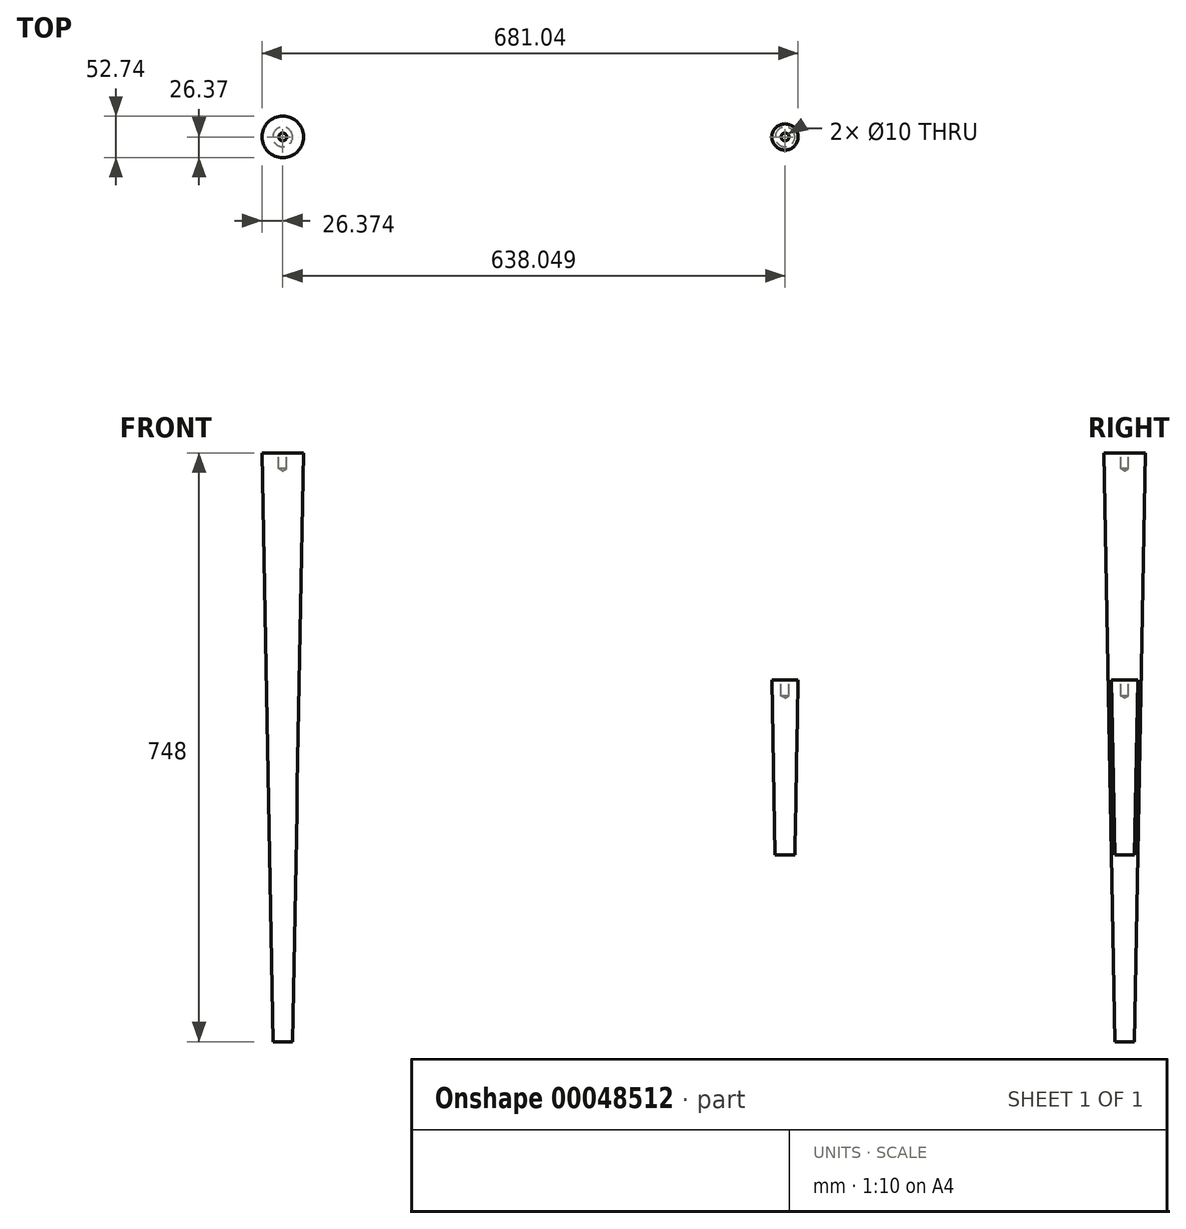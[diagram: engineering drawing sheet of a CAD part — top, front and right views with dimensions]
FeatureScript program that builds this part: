
annotation { "Feature Type Name" : "Feature", "Feature Type Description" : "" }
export const myFeature = defineFeature(function(context is Context, id is Id, definition is map)
    precondition{}
    {
        {
            var Q0;
            Q0=qCreatedBy(makeId("Front.planeOp"),FACE);
            var sketch = newSketch(context, id + "F0", { "sketchPlane" : qUnion([Q0])});
            skLineSegment(sketch, "E0.bottom", {"start": v(-272.94, 167.73) * mm, "end": v(-222.94, 167.73) * mm});
            skLineSegment(sketch, "E0.top", {"start": v(-272.94, -506.27) * mm, "end": v(-222.94, -506.27) * mm});
            skLineSegment(sketch, "E0.left", {"start": v(-272.94, 167.73) * mm, "end": v(-272.94, -506.27) * mm});
            skLineSegment(sketch, "E0.right", {"start": v(-222.94, 167.73) * mm, "end": v(-222.94, -506.27) * mm});
            skLineSegment(sketch, "E1", {"start": v(-247.94, 167.73) * mm, "end": v(-247.94, -506.27) * mm});
            skLineSegment(sketch, "E2", {"start": v(-247.94, -506.27) * mm, "end": v(-260.44, -506.27) * mm});
            skLineSegment(sketch, "E3", {"start": v(-272.94, 167.73) * mm, "end": v(-260.44, -506.27) * mm});
            skLineSegment(sketch, "E4.top", {"start": v(-272.94, 241.73) * mm, "end": v(-222.94, 241.73) * mm});
            skLineSegment(sketch, "E4.left", {"start": v(-272.94, 167.73) * mm, "end": v(-272.94, 241.73) * mm});
            skLineSegment(sketch, "E4.right", {"start": v(-222.94, 167.73) * mm, "end": v(-222.94, 241.73) * mm});
            skLineSegment(sketch, "E5", {"start": v(-272.94, 167.73) * mm, "end": v(-274.3, 241.73) * mm});
            skLineSegment(sketch, "E6", {"start": v(-274.3, 241.73) * mm, "end": v(-247.94, 241.73) * mm});
            skLineSegment(sketch, "E7", {"start": v(-247.94, 241.73) * mm, "end": v(-247.94, 167.73) * mm});
            skLineSegment(sketch, "E8.bottom", {"start": v(-222.94, -506.27) * mm, "end": v(-272.94, -506.27) * mm});
            skLineSegment(sketch, "E8.top", {"start": v(-222.94, -284.27) * mm, "end": v(-272.94, -284.27) * mm});
            skLineSegment(sketch, "E8.left", {"start": v(-222.94, -506.27) * mm, "end": v(-222.94, -284.27) * mm});
            skLineSegment(sketch, "E8.right", {"start": v(-272.94, -506.27) * mm, "end": v(-272.94, -284.27) * mm});
            skSolve(sketch);
        }
        {
            var Q0;
            {var subQ0=sQuery(id+"F0.wireOp",EDGE,"E4.left");Q0=makeQuery(id+"F0.imprint","IMPRINT",FACE,{"disambiguationData":[TD([[makeQuery(id+"F0.imprint","IMPRINT",EDGE,{"derivedFrom":subQ0}),1.0]])]});}
            var Q1;
            {var subQ0=sQuery(id+"F0.wireOp",EDGE,"E4.left");Q1=makeQuery(id+"F0.imprint","IMPRINT",FACE,{"disambiguationData":[TD([[makeQuery(id+"F0.imprint","IMPRINT",EDGE,{"derivedFrom":subQ0}),-1.0]])]});}
            var Q2;
            {var subQ0=sQuery(id+"F0.wireOp",EDGE,"E1");Q2=makeQuery(id+"F0.imprint","IMPRINT",FACE,{"disambiguationData":[TD([[makeQuery(id+"F0.imprint","IMPRINT",EDGE,{"derivedFrom":subQ0}),-1.0]])]});}
            var Q3;
            Q3=sQuery(id+"F0.wireOp",EDGE,"E7");
            revolve(context, id + "F1", {"entities" : qUnion([Q0, Q1, Q2]), "axis" : qUnion([Q3]), "revolveType" : RevolveType.FULL});
        }
        {
            var Q0;
            Q0=qCreatedBy(makeId("Front.planeOp"),FACE);
            var sketch = newSketch(context, id + "F2", { "sketchPlane" : qUnion([Q0])});
            skLineSegment(sketch, "E9.top", {"start": v(365.11, -268.83) * mm, "end": v(415.11, -268.83) * mm});
            skLineSegment(sketch, "E9.left", {"start": v(365.11, 405.17) * mm, "end": v(365.11, -268.83) * mm});
            skLineSegment(sketch, "E10", {"start": v(390.11, 405.17) * mm, "end": v(390.11, -268.83) * mm});
            skLineSegment(sketch, "E11", {"start": v(365.11, 405.17) * mm, "end": v(377.61, -268.83) * mm});
            skLineSegment(sketch, "E12.top", {"start": v(415.11, -46.83) * mm, "end": v(365.11, -46.83) * mm});
            skLineSegment(sketch, "E12.left", {"start": v(415.11, -268.83) * mm, "end": v(415.11, -46.83) * mm});
            skSolve(sketch);
        }
        {
            var Q0;
            {var subQ0=sQuery(id+"F2.wireOp",EDGE,"E10");var subQ1=sQuery(id+"F2.wireOp",EDGE,"E9.top");var subQ2=makeQuery(id+"F2.imprint","INTERSECT",VERTEX,{"derivedFrom":[subQ1,subQ0]});Q0=makeQuery(id+"F2.imprint","IMPRINT",FACE,{"disambiguationData":[TD([[makeQuery(id+"F2.imprint","IMPRINT",EDGE,{"disambiguationData":[TD([[subQ2,1.0]])],"derivedFrom":subQ1}),1.0]])]});}
            var Q1;
            Q1=sQuery(id+"F2.wireOp",EDGE,"E10");
            revolve(context, id + "F3", {"entities" : qUnion([Q0]), "axis" : qUnion([Q1]), "revolveType" : RevolveType.FULL});
        }
        {
            var Q0;
            Q0=makeQuery(id+"F1.opRevolve","SWEPT_FACE",FACE,{"disambiguationData":[OSD([sQuery(id+"F0.wireOp",EDGE,"E6")])]});
            var sketch = newSketch(context, id + "F4", { "sketchPlane" : qUnion([Q0])});
            skPoint(sketch, "E13", {"position": v(-247.94, 0) * mm});
            skSolve(sketch);
        }
        {
            var Q0;
            Q0=sQuery(id+"F4.wireOp",VERTEX,"E13");
            var Q1;
            Q1=makeQuery(id+"F1.opRevolve","SWEPT_BODY",BODY,{"disambiguationData":[OSD([sQuery(id+"F0.wireOp",EDGE,"E1"),sQuery(id+"F0.wireOp",EDGE,"E3"),sQuery(id+"F0.wireOp",EDGE,"E5"),sQuery(id+"F0.wireOp",EDGE,"E6"),sQuery(id+"F0.wireOp",EDGE,"E7"),sQuery(id+"F0.wireOp",EDGE,"E8.bottom")])]});
            hole(context, id + "F5", {"style" : HoleStyle.SIMPLE, "endStyle" : HoleEndStyle.BLIND, "holeDiameter" : 10 * mm, "holeDepth" : 20 * mm, "locations" : qUnion([Q0]), "scope" : qUnion([Q1])});
        }
        {
            var Q0;
            Q0=makeQuery(id+"F3.opRevolve","SWEPT_FACE",FACE,{"disambiguationData":[OSD([sQuery(id+"F2.wireOp",EDGE,"E12.top")])]});
            var sketch = newSketch(context, id + "F6", { "sketchPlane" : qUnion([Q0])});
            skPoint(sketch, "E14", {"position": v(390.11, 0) * mm});
            skSolve(sketch);
        }
        {
            var Q0;
            Q0=sQuery(id+"F6.wireOp",VERTEX,"E14");
            var Q1;
            Q1=makeQuery(id+"F3.opRevolve","SWEPT_BODY",BODY,{"disambiguationData":[OSD([sQuery(id+"F2.wireOp",EDGE,"E9.top"),sQuery(id+"F2.wireOp",EDGE,"E10"),sQuery(id+"F2.wireOp",EDGE,"E11"),sQuery(id+"F2.wireOp",EDGE,"E12.top")])]});
            hole(context, id + "F7", {"style" : HoleStyle.SIMPLE, "endStyle" : HoleEndStyle.BLIND, "holeDiameter" : 10 * mm, "holeDepth" : 20 * mm, "locations" : qUnion([Q0]), "scope" : qUnion([Q1])});
        }
    });
